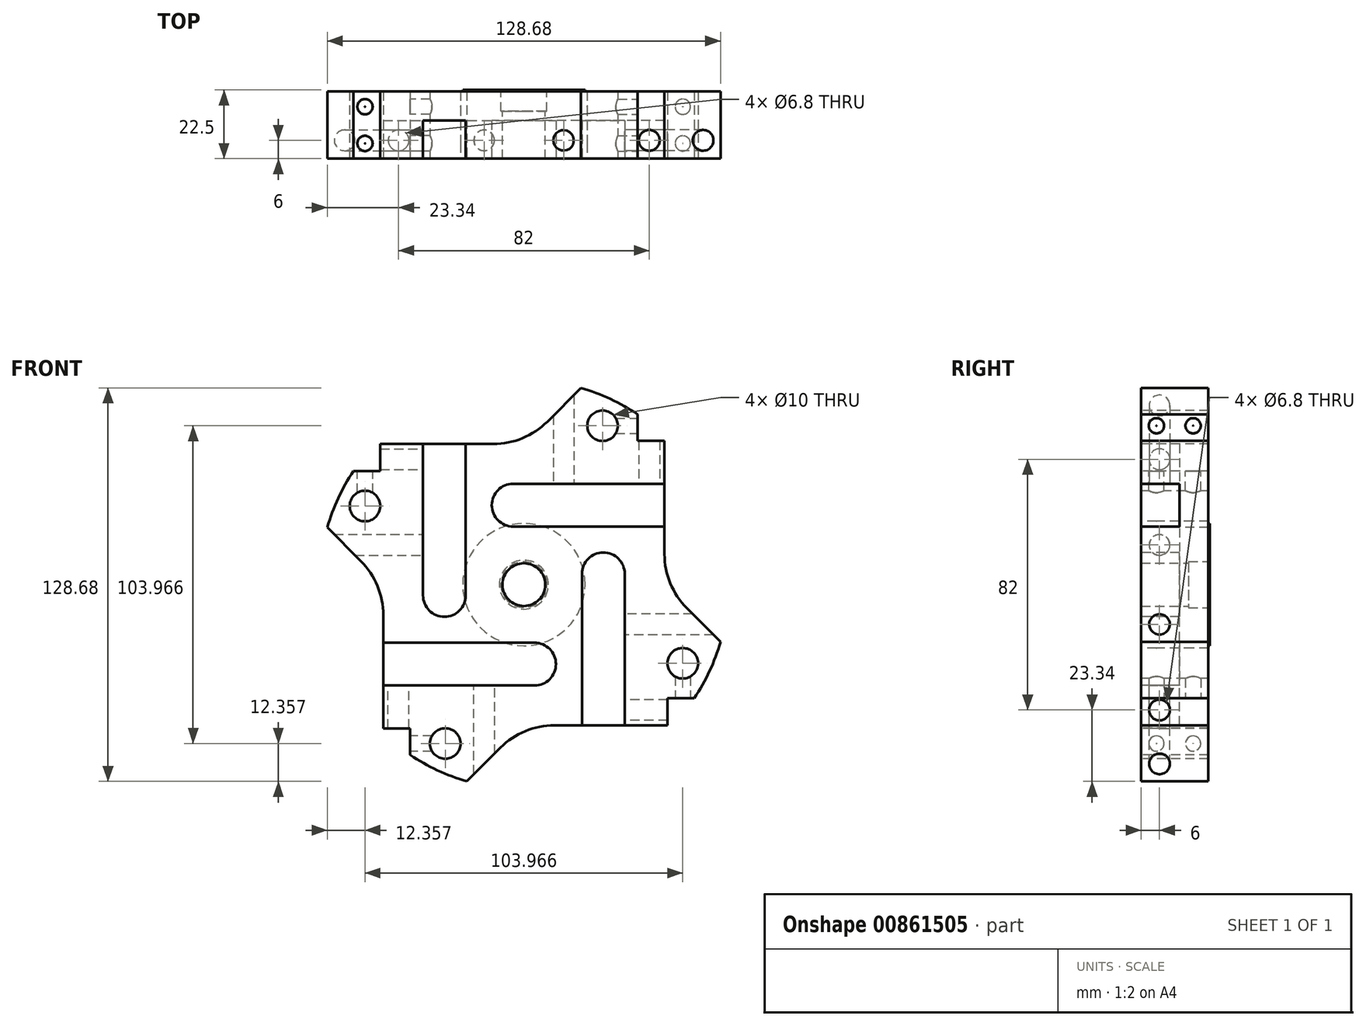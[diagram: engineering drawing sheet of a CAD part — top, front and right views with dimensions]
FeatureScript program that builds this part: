
annotation { "Feature Type Name" : "Feature", "Feature Type Description" : "" }
export const myFeature = defineFeature(function(context is Context, id is Id, definition is map)
    precondition{}
    {
        {
            var Q0;
            Q0=qCreatedBy(makeId("Front.planeOp"),FACE);
            var sketch = newSketch(context, id + "F0", { "sketchPlane" : qUnion([Q0])});
            skLineSegment(sketch, "E0", {"start": v(-46, -10) * mm, "end": v(-46, -47) * mm});
            skLineSegment(sketch, "E1", {"start": v(-37.2, -47) * mm, "end": v(-37.2, -55.72) * mm});
            skLineSegment(sketch, "E2", {"start": v(-46, -47) * mm, "end": v(-37.2, -47) * mm});
            skArc(sketch, "E3.trimOffspring", {"start": v(-46, -10) * mm, "mid": v(-47.9, -0.43) * mm, "end": v(-53.32, 7.68) * mm});
            skLineSegment(sketch, "E4", {"start": v(-53.32, 7.68) * mm, "end": v(-64.34, 18.7) * mm});
            skArc(sketch, "E5", {"start": v(-37.2, -55.72) * mm, "mid": v(-28.28, -60.74) * mm, "end": v(-18.7, -64.34) * mm});
            skLineSegment(sketch, "E6", {"start": v(-71, -10) * mm, "end": v(-46, -10) * mm, "construction": true});
            skLineSegment(sketch, "E7", {"start": v(-71, -10) * mm, "end": v(-53.32, 7.68) * mm, "construction": true});
            skLineSegment(sketch, "E8.1.0", {"start": v(-7.68, -53.32) * mm, "end": v(-18.7, -64.34) * mm});
            skArc(sketch, "E8.1.1", {"start": v(10, -46) * mm, "mid": v(0.43, -47.9) * mm, "end": v(-7.68, -53.32) * mm});
            skLineSegment(sketch, "E8.1.2", {"start": v(10, -46) * mm, "end": v(47, -46) * mm});
            skLineSegment(sketch, "E8.1.3", {"start": v(47, -46) * mm, "end": v(47, -37.2) * mm});
            skLineSegment(sketch, "E8.1.4", {"start": v(47, -37.2) * mm, "end": v(55.72, -37.2) * mm});
            skLineSegment(sketch, "E8.2.0", {"start": v(53.32, -7.68) * mm, "end": v(64.34, -18.7) * mm});
            skArc(sketch, "E8.2.1", {"start": v(46, 10) * mm, "mid": v(47.9, 0.43) * mm, "end": v(53.32, -7.68) * mm});
            skLineSegment(sketch, "E8.2.2", {"start": v(46, 10) * mm, "end": v(46, 47) * mm});
            skLineSegment(sketch, "E8.2.3", {"start": v(46, 47) * mm, "end": v(37.2, 47) * mm});
            skLineSegment(sketch, "E8.2.4", {"start": v(37.2, 47) * mm, "end": v(37.2, 55.72) * mm});
            skLineSegment(sketch, "E8.3.0", {"start": v(7.68, 53.32) * mm, "end": v(18.7, 64.34) * mm});
            skArc(sketch, "E8.3.1", {"start": v(-10, 46) * mm, "mid": v(-0.43, 47.9) * mm, "end": v(7.68, 53.32) * mm});
            skLineSegment(sketch, "E8.3.2", {"start": v(-10, 46) * mm, "end": v(-47, 46) * mm});
            skLineSegment(sketch, "E8.3.3", {"start": v(-47, 46) * mm, "end": v(-47, 37.2) * mm});
            skLineSegment(sketch, "E8.3.4", {"start": v(-47, 37.2) * mm, "end": v(-55.72, 37.2) * mm});
            skArc(sketch, "E9.trimOffspring", {"start": v(-55.72, 37.2) * mm, "mid": v(-60.74, 28.28) * mm, "end": v(-64.34, 18.7) * mm});
            skArc(sketch, "E10.trimOffspring", {"start": v(37.2, 55.72) * mm, "mid": v(28.28, 60.74) * mm, "end": v(18.7, 64.34) * mm});
            skArc(sketch, "E11.trimOffspring", {"start": v(55.72, -37.2) * mm, "mid": v(60.74, -28.28) * mm, "end": v(64.34, -18.7) * mm});
            skLineSegment(sketch, "E12", {"start": v(0, 0) * mm, "end": v(-51.98, 25.73) * mm});
            skCircle(sketch, "E13", {"center": v(-51.98, 25.73) * mm, "radius": 5 * mm});
            skCircle(sketch, "E14.1.0", {"center": v(-25.73, -51.98) * mm, "radius": 5 * mm});
            skCircle(sketch, "E14.2.0", {"center": v(51.98, -25.73) * mm, "radius": 5 * mm});
            skCircle(sketch, "E14.3.0", {"center": v(25.73, 51.98) * mm, "radius": 5 * mm});
            skSolve(sketch);
        }
        {
            var Q0;
            Q0 = qSketchRegion(id + "F0", true);
            extrude(context, id + "F1", {"entities" : qUnion([Q0]), "oppositeDirection" : true, "depth" : 22 * mm, "offsetDistance" : 25 * mm});
        }
        {
            var Q0;
            Q0=makeQuery(id+"F1.opExtrude","CAP_FACE",FACE,{"disambiguationData":[OSD([sQuery(id+"F0.wireOp",EDGE,"E0"),sQuery(id+"F0.wireOp",EDGE,"E1"),sQuery(id+"F0.wireOp",EDGE,"E2"),sQuery(id+"F0.wireOp",EDGE,"E3.trimOffspring"),sQuery(id+"F0.wireOp",EDGE,"E4"),sQuery(id+"F0.wireOp",EDGE,"E5"),sQuery(id+"F0.wireOp",EDGE,"E8.1.0"),sQuery(id+"F0.wireOp",EDGE,"E8.1.1"),sQuery(id+"F0.wireOp",EDGE,"E8.1.2"),sQuery(id+"F0.wireOp",EDGE,"E8.1.3"),sQuery(id+"F0.wireOp",EDGE,"E8.1.4"),sQuery(id+"F0.wireOp",EDGE,"E8.2.0"),sQuery(id+"F0.wireOp",EDGE,"E8.2.1"),sQuery(id+"F0.wireOp",EDGE,"E8.2.2"),sQuery(id+"F0.wireOp",EDGE,"E8.2.3"),sQuery(id+"F0.wireOp",EDGE,"E8.2.4"),sQuery(id+"F0.wireOp",EDGE,"E8.3.0"),sQuery(id+"F0.wireOp",EDGE,"E8.3.1"),sQuery(id+"F0.wireOp",EDGE,"E8.3.2"),sQuery(id+"F0.wireOp",EDGE,"E8.3.3"),sQuery(id+"F0.wireOp",EDGE,"E8.3.4"),sQuery(id+"F0.wireOp",EDGE,"E9.trimOffspring"),sQuery(id+"F0.wireOp",EDGE,"E10.trimOffspring"),sQuery(id+"F0.wireOp",EDGE,"E11.trimOffspring"),sQuery(id+"F0.wireOp",EDGE,"E13"),sQuery(id+"F0.wireOp",EDGE,"E14.1.0"),sQuery(id+"F0.wireOp",EDGE,"E14.2.0"),sQuery(id+"F0.wireOp",EDGE,"E14.3.0")])],"isStart":false});
            var sketch = newSketch(context, id + "F2", { "sketchPlane" : qUnion([Q0])});
            skCircle(sketch, "E15", {"center": v(0, 0) * mm, "radius": 20 * mm});
            skSolve(sketch);
        }
        {
            var Q0;
            Q0 = qSketchRegion(id + "F2", true);
            extrude(context, id + "F3", {"entities" : qUnion([Q0]), "operationType" : NewBodyOperationType.ADD, "depth" : .5 * mm, "offsetDistance" : 25 * mm});
        }
        {
            var Q0;
            Q0=makeQuery(id+"F1.opExtrude","SWEPT_FACE",FACE,{"disambiguationData":[OSD([sQuery(id+"F0.wireOp",EDGE,"E8.2.4")])]});
            var sketch = newSketch(context, id + "F4", { "sketchPlane" : qUnion([Q0])});
            skPoint(sketch, "E16", {"position": v(5, 51.98) * mm});
            skPoint(sketch, "E17", {"position": v(17, 51.98) * mm});
            skSolve(sketch);
        }
        {
            var Q0;
            Q0=sQuery(id+"F4.wireOp",VERTEX,"E16");
            var Q1;
            Q1=sQuery(id+"F4.wireOp",VERTEX,"E17");
            var Q2;
            Q2=makeQuery(id+"F1.opExtrude","SWEPT_BODY",BODY,{"disambiguationData":[OSD([sQuery(id+"F0.wireOp",EDGE,"E0"),sQuery(id+"F0.wireOp",EDGE,"E1"),sQuery(id+"F0.wireOp",EDGE,"E2"),sQuery(id+"F0.wireOp",EDGE,"E3.trimOffspring"),sQuery(id+"F0.wireOp",EDGE,"E4"),sQuery(id+"F0.wireOp",EDGE,"E5"),sQuery(id+"F0.wireOp",EDGE,"E8.1.0"),sQuery(id+"F0.wireOp",EDGE,"E8.1.1"),sQuery(id+"F0.wireOp",EDGE,"E8.1.2"),sQuery(id+"F0.wireOp",EDGE,"E8.1.3"),sQuery(id+"F0.wireOp",EDGE,"E8.1.4"),sQuery(id+"F0.wireOp",EDGE,"E8.2.0"),sQuery(id+"F0.wireOp",EDGE,"E8.2.1"),sQuery(id+"F0.wireOp",EDGE,"E8.2.2"),sQuery(id+"F0.wireOp",EDGE,"E8.2.3"),sQuery(id+"F0.wireOp",EDGE,"E8.2.4"),sQuery(id+"F0.wireOp",EDGE,"E8.3.0"),sQuery(id+"F0.wireOp",EDGE,"E8.3.1"),sQuery(id+"F0.wireOp",EDGE,"E8.3.2"),sQuery(id+"F0.wireOp",EDGE,"E8.3.3"),sQuery(id+"F0.wireOp",EDGE,"E8.3.4"),sQuery(id+"F0.wireOp",EDGE,"E9.trimOffspring"),sQuery(id+"F0.wireOp",EDGE,"E10.trimOffspring"),sQuery(id+"F0.wireOp",EDGE,"E11.trimOffspring"),sQuery(id+"F0.wireOp",EDGE,"E13"),sQuery(id+"F0.wireOp",EDGE,"E14.1.0"),sQuery(id+"F0.wireOp",EDGE,"E14.2.0"),sQuery(id+"F0.wireOp",EDGE,"E14.3.0")])]});
            hole(context, id + "F5", {"style" : HoleStyle.SIMPLE, "endStyle" : HoleEndStyle.BLIND, "standardTappedOrClearance" : lookupTablePath({ "standard" : "ISO", "engagement" : "75%", "pitch" : "1 mm", "size" : "M6", "type" : "Tapped" }), "standardBlindInLast" : lookupTablePath({ "standard" : "ISO", "engagement" : "75%", "pitch" : "1 mm", "size" : "M6", "type" : "Tapped" }), "holeDiameter" : 5 * mm, "majorDiameter" : 6 * mm, "showTappedDepth" : true, "holeDepth" : 15 * mm, "isTappedThrough" : true, "tappedDepth" : 12 * mm, "tapClearance" : 3, "startFromSketch" : true, "locations" : qUnion([Q0, Q1]), "scope" : qUnion([Q2])});
        }
        {
            var Q0;
            Q0=makeQuery(id+"F1.opExtrude","SWEPT_FACE",FACE,{"disambiguationData":[OSD([sQuery(id+"F0.wireOp",EDGE,"E8.3.4")])]});
            var sketch = newSketch(context, id + "F6", { "sketchPlane" : qUnion([Q0])});
            skPoint(sketch, "E18", {"position": v(-51.98, 5) * mm});
            skPoint(sketch, "E19", {"position": v(-51.98, 17) * mm});
            skSolve(sketch);
        }
        {
            var Q0;
            Q0=sQuery(id+"F6.wireOp",VERTEX,"E19");
            var Q1;
            Q1=sQuery(id+"F6.wireOp",VERTEX,"E18");
            var Q2;
            Q2=makeQuery(id+"F1.opExtrude","SWEPT_BODY",BODY,{"disambiguationData":[OSD([sQuery(id+"F0.wireOp",EDGE,"E0"),sQuery(id+"F0.wireOp",EDGE,"E1"),sQuery(id+"F0.wireOp",EDGE,"E2"),sQuery(id+"F0.wireOp",EDGE,"E3.trimOffspring"),sQuery(id+"F0.wireOp",EDGE,"E4"),sQuery(id+"F0.wireOp",EDGE,"E5"),sQuery(id+"F0.wireOp",EDGE,"E8.1.0"),sQuery(id+"F0.wireOp",EDGE,"E8.1.1"),sQuery(id+"F0.wireOp",EDGE,"E8.1.2"),sQuery(id+"F0.wireOp",EDGE,"E8.1.3"),sQuery(id+"F0.wireOp",EDGE,"E8.1.4"),sQuery(id+"F0.wireOp",EDGE,"E8.2.0"),sQuery(id+"F0.wireOp",EDGE,"E8.2.1"),sQuery(id+"F0.wireOp",EDGE,"E8.2.2"),sQuery(id+"F0.wireOp",EDGE,"E8.2.3"),sQuery(id+"F0.wireOp",EDGE,"E8.2.4"),sQuery(id+"F0.wireOp",EDGE,"E8.3.0"),sQuery(id+"F0.wireOp",EDGE,"E8.3.1"),sQuery(id+"F0.wireOp",EDGE,"E8.3.2"),sQuery(id+"F0.wireOp",EDGE,"E8.3.3"),sQuery(id+"F0.wireOp",EDGE,"E8.3.4"),sQuery(id+"F0.wireOp",EDGE,"E9.trimOffspring"),sQuery(id+"F0.wireOp",EDGE,"E10.trimOffspring"),sQuery(id+"F0.wireOp",EDGE,"E11.trimOffspring"),sQuery(id+"F0.wireOp",EDGE,"E13"),sQuery(id+"F0.wireOp",EDGE,"E14.1.0"),sQuery(id+"F0.wireOp",EDGE,"E14.2.0"),sQuery(id+"F0.wireOp",EDGE,"E14.3.0")])]});
            hole(context, id + "F7", {"style" : HoleStyle.SIMPLE, "endStyle" : HoleEndStyle.BLIND, "standardTappedOrClearance" : lookupTablePath({ "standard" : "ISO", "engagement" : "75%", "pitch" : "1 mm", "size" : "M6", "type" : "Tapped" }), "standardBlindInLast" : lookupTablePath({ "standard" : "ISO", "engagement" : "75%", "pitch" : "1 mm", "size" : "M6", "type" : "Tapped" }), "holeDiameter" : 5 * mm, "majorDiameter" : 6 * mm, "showTappedDepth" : true, "holeDepth" : 15 * mm, "isTappedThrough" : true, "tappedDepth" : 12 * mm, "tapClearance" : 3, "startFromSketch" : true, "locations" : qUnion([Q0, Q1]), "scope" : qUnion([Q2])});
        }
        {
            var Q0;
            Q0=makeQuery(id+"F1.opExtrude","SWEPT_FACE",FACE,{"disambiguationData":[OSD([sQuery(id+"F0.wireOp",EDGE,"E1")])]});
            var sketch = newSketch(context, id + "F8", { "sketchPlane" : qUnion([Q0])});
            skPoint(sketch, "E20", {"position": v(-5, -51.98) * mm});
            skPoint(sketch, "E21", {"position": v(-17, -51.98) * mm});
            skSolve(sketch);
        }
        {
            var Q0;
            Q0=sQuery(id+"F8.wireOp",VERTEX,"E20");
            var Q1;
            Q1=sQuery(id+"F8.wireOp",VERTEX,"E21");
            var Q2;
            Q2=makeQuery(id+"F1.opExtrude","SWEPT_BODY",BODY,{"disambiguationData":[OSD([sQuery(id+"F0.wireOp",EDGE,"E0"),sQuery(id+"F0.wireOp",EDGE,"E1"),sQuery(id+"F0.wireOp",EDGE,"E2"),sQuery(id+"F0.wireOp",EDGE,"E3.trimOffspring"),sQuery(id+"F0.wireOp",EDGE,"E4"),sQuery(id+"F0.wireOp",EDGE,"E5"),sQuery(id+"F0.wireOp",EDGE,"E8.1.0"),sQuery(id+"F0.wireOp",EDGE,"E8.1.1"),sQuery(id+"F0.wireOp",EDGE,"E8.1.2"),sQuery(id+"F0.wireOp",EDGE,"E8.1.3"),sQuery(id+"F0.wireOp",EDGE,"E8.1.4"),sQuery(id+"F0.wireOp",EDGE,"E8.2.0"),sQuery(id+"F0.wireOp",EDGE,"E8.2.1"),sQuery(id+"F0.wireOp",EDGE,"E8.2.2"),sQuery(id+"F0.wireOp",EDGE,"E8.2.3"),sQuery(id+"F0.wireOp",EDGE,"E8.2.4"),sQuery(id+"F0.wireOp",EDGE,"E8.3.0"),sQuery(id+"F0.wireOp",EDGE,"E8.3.1"),sQuery(id+"F0.wireOp",EDGE,"E8.3.2"),sQuery(id+"F0.wireOp",EDGE,"E8.3.3"),sQuery(id+"F0.wireOp",EDGE,"E8.3.4"),sQuery(id+"F0.wireOp",EDGE,"E9.trimOffspring"),sQuery(id+"F0.wireOp",EDGE,"E10.trimOffspring"),sQuery(id+"F0.wireOp",EDGE,"E11.trimOffspring"),sQuery(id+"F0.wireOp",EDGE,"E13"),sQuery(id+"F0.wireOp",EDGE,"E14.1.0"),sQuery(id+"F0.wireOp",EDGE,"E14.2.0"),sQuery(id+"F0.wireOp",EDGE,"E14.3.0")])]});
            hole(context, id + "F9", {"style" : HoleStyle.SIMPLE, "endStyle" : HoleEndStyle.BLIND, "standardTappedOrClearance" : lookupTablePath({ "standard" : "ISO", "engagement" : "75%", "pitch" : "1 mm", "size" : "M6", "type" : "Tapped" }), "standardBlindInLast" : lookupTablePath({ "standard" : "ISO", "engagement" : "75%", "pitch" : "1 mm", "size" : "M6", "type" : "Tapped" }), "holeDiameter" : 5 * mm, "majorDiameter" : 6 * mm, "showTappedDepth" : true, "holeDepth" : 15 * mm, "isTappedThrough" : true, "tappedDepth" : 12 * mm, "tapClearance" : 3, "startFromSketch" : true, "locations" : qUnion([Q0, Q1]), "scope" : qUnion([Q2])});
        }
        {
            var Q0;
            Q0=makeQuery(id+"F1.opExtrude","SWEPT_FACE",FACE,{"disambiguationData":[OSD([sQuery(id+"F0.wireOp",EDGE,"E8.1.4")])]});
            var sketch = newSketch(context, id + "F10", { "sketchPlane" : qUnion([Q0])});
            skPoint(sketch, "E22", {"position": v(51.98, -5) * mm});
            skPoint(sketch, "E23", {"position": v(51.98, -17) * mm});
            skSolve(sketch);
        }
        {
            var Q0;
            Q0=sQuery(id+"F10.wireOp",VERTEX,"E22");
            var Q1;
            Q1=sQuery(id+"F10.wireOp",VERTEX,"E23");
            var Q2;
            Q2=makeQuery(id+"F1.opExtrude","SWEPT_BODY",BODY,{"disambiguationData":[OSD([sQuery(id+"F0.wireOp",EDGE,"E0"),sQuery(id+"F0.wireOp",EDGE,"E1"),sQuery(id+"F0.wireOp",EDGE,"E2"),sQuery(id+"F0.wireOp",EDGE,"E3.trimOffspring"),sQuery(id+"F0.wireOp",EDGE,"E4"),sQuery(id+"F0.wireOp",EDGE,"E5"),sQuery(id+"F0.wireOp",EDGE,"E8.1.0"),sQuery(id+"F0.wireOp",EDGE,"E8.1.1"),sQuery(id+"F0.wireOp",EDGE,"E8.1.2"),sQuery(id+"F0.wireOp",EDGE,"E8.1.3"),sQuery(id+"F0.wireOp",EDGE,"E8.1.4"),sQuery(id+"F0.wireOp",EDGE,"E8.2.0"),sQuery(id+"F0.wireOp",EDGE,"E8.2.1"),sQuery(id+"F0.wireOp",EDGE,"E8.2.2"),sQuery(id+"F0.wireOp",EDGE,"E8.2.3"),sQuery(id+"F0.wireOp",EDGE,"E8.2.4"),sQuery(id+"F0.wireOp",EDGE,"E8.3.0"),sQuery(id+"F0.wireOp",EDGE,"E8.3.1"),sQuery(id+"F0.wireOp",EDGE,"E8.3.2"),sQuery(id+"F0.wireOp",EDGE,"E8.3.3"),sQuery(id+"F0.wireOp",EDGE,"E8.3.4"),sQuery(id+"F0.wireOp",EDGE,"E9.trimOffspring"),sQuery(id+"F0.wireOp",EDGE,"E10.trimOffspring"),sQuery(id+"F0.wireOp",EDGE,"E11.trimOffspring"),sQuery(id+"F0.wireOp",EDGE,"E13"),sQuery(id+"F0.wireOp",EDGE,"E14.1.0"),sQuery(id+"F0.wireOp",EDGE,"E14.2.0"),sQuery(id+"F0.wireOp",EDGE,"E14.3.0")])]});
            hole(context, id + "F11", {"style" : HoleStyle.SIMPLE, "endStyle" : HoleEndStyle.BLIND, "standardTappedOrClearance" : lookupTablePath({ "standard" : "ISO", "engagement" : "75%", "pitch" : "1 mm", "size" : "M6", "type" : "Tapped" }), "standardBlindInLast" : lookupTablePath({ "standard" : "ISO", "engagement" : "75%", "pitch" : "1 mm", "size" : "M6", "type" : "Tapped" }), "holeDiameter" : 5 * mm, "majorDiameter" : 6 * mm, "showTappedDepth" : true, "holeDepth" : 15 * mm, "isTappedThrough" : true, "tappedDepth" : 12 * mm, "tapClearance" : 3, "startFromSketch" : true, "locations" : qUnion([Q0, Q1]), "scope" : qUnion([Q2])});
        }
        {
            var Q0;
            Q0=makeQuery(id+"F1.opExtrude","CAP_FACE",FACE,{"disambiguationData":[OSD([sQuery(id+"F0.wireOp",EDGE,"E0"),sQuery(id+"F0.wireOp",EDGE,"E1"),sQuery(id+"F0.wireOp",EDGE,"E2"),sQuery(id+"F0.wireOp",EDGE,"E3.trimOffspring"),sQuery(id+"F0.wireOp",EDGE,"E4"),sQuery(id+"F0.wireOp",EDGE,"E5"),sQuery(id+"F0.wireOp",EDGE,"E8.1.0"),sQuery(id+"F0.wireOp",EDGE,"E8.1.1"),sQuery(id+"F0.wireOp",EDGE,"E8.1.2"),sQuery(id+"F0.wireOp",EDGE,"E8.1.3"),sQuery(id+"F0.wireOp",EDGE,"E8.1.4"),sQuery(id+"F0.wireOp",EDGE,"E8.2.0"),sQuery(id+"F0.wireOp",EDGE,"E8.2.1"),sQuery(id+"F0.wireOp",EDGE,"E8.2.2"),sQuery(id+"F0.wireOp",EDGE,"E8.2.3"),sQuery(id+"F0.wireOp",EDGE,"E8.2.4"),sQuery(id+"F0.wireOp",EDGE,"E8.3.0"),sQuery(id+"F0.wireOp",EDGE,"E8.3.1"),sQuery(id+"F0.wireOp",EDGE,"E8.3.2"),sQuery(id+"F0.wireOp",EDGE,"E8.3.3"),sQuery(id+"F0.wireOp",EDGE,"E8.3.4"),sQuery(id+"F0.wireOp",EDGE,"E9.trimOffspring"),sQuery(id+"F0.wireOp",EDGE,"E10.trimOffspring"),sQuery(id+"F0.wireOp",EDGE,"E11.trimOffspring"),sQuery(id+"F0.wireOp",EDGE,"E13"),sQuery(id+"F0.wireOp",EDGE,"E14.1.0"),sQuery(id+"F0.wireOp",EDGE,"E14.2.0"),sQuery(id+"F0.wireOp",EDGE,"E14.3.0")])],"isStart":true});
            var sketch = newSketch(context, id + "F12", { "sketchPlane" : qUnion([Q0])});
            skLineSegment(sketch, "E24", {"start": v(19, -46) * mm, "end": v(19, 3.5) * mm});
            skLineSegment(sketch, "E25", {"start": v(26, 10.5) * mm, "end": v(26, 10.5) * mm});
            skLineSegment(sketch, "E26", {"start": v(33, 3.5) * mm, "end": v(33, -46) * mm});
            skLineSegment(sketch, "E27", {"start": v(33, -46) * mm, "end": v(19, -46) * mm});
            skPoint(sketch, "E28.visualSharp", {"position": v(19, 10.5) * mm});
            skArc(sketch, "E28.filletArc", {"start": v(26, 10.5) * mm, "mid": v(21.05, 8.45) * mm, "end": v(19, 3.5) * mm});
            skPoint(sketch, "E29.visualSharp", {"position": v(33, 10.5) * mm});
            skArc(sketch, "E29.filletArc", {"start": v(33, 3.5) * mm, "mid": v(30.95, 8.45) * mm, "end": v(26, 10.5) * mm});
            skLineSegment(sketch, "E30.1.0", {"start": v(46, 19) * mm, "end": v(-3.5, 19) * mm});
            skLineSegment(sketch, "E30.1.1", {"start": v(46, 33) * mm, "end": v(46, 19) * mm});
            skLineSegment(sketch, "E30.1.2", {"start": v(-3.5, 33) * mm, "end": v(46, 33) * mm});
            skArc(sketch, "E30.1.3", {"start": v(-3.5, 33) * mm, "mid": v(-8.45, 30.95) * mm, "end": v(-10.5, 26) * mm});
            skArc(sketch, "E30.1.4", {"start": v(-10.5, 26) * mm, "mid": v(-8.45, 21.05) * mm, "end": v(-3.5, 19) * mm});
            skLineSegment(sketch, "E30.2.0", {"start": v(-19, 46) * mm, "end": v(-19, -3.5) * mm});
            skLineSegment(sketch, "E30.2.1", {"start": v(-33, 46) * mm, "end": v(-19, 46) * mm});
            skLineSegment(sketch, "E30.2.2", {"start": v(-33, -3.5) * mm, "end": v(-33, 46) * mm});
            skArc(sketch, "E30.2.3", {"start": v(-33, -3.5) * mm, "mid": v(-30.95, -8.45) * mm, "end": v(-26, -10.5) * mm});
            skArc(sketch, "E30.2.4", {"start": v(-26, -10.5) * mm, "mid": v(-21.05, -8.45) * mm, "end": v(-19, -3.5) * mm});
            skLineSegment(sketch, "E30.3.0", {"start": v(-46, -19) * mm, "end": v(3.5, -19) * mm});
            skLineSegment(sketch, "E30.3.1", {"start": v(-46, -33) * mm, "end": v(-46, -19) * mm});
            skLineSegment(sketch, "E30.3.2", {"start": v(3.5, -33) * mm, "end": v(-46, -33) * mm});
            skArc(sketch, "E30.3.3", {"start": v(3.5, -33) * mm, "mid": v(8.45, -30.95) * mm, "end": v(10.5, -26) * mm});
            skArc(sketch, "E30.3.4", {"start": v(10.5, -26) * mm, "mid": v(8.45, -21.05) * mm, "end": v(3.5, -19) * mm});
            skPoint(sketch, "E30.center", {"position": v(0, 0) * mm});
            skSolve(sketch);
        }
        {
            var Q0;
            Q0 = qSketchRegion(id + "F12", true);
            extrude(context, id + "F13", {"entities" : qUnion([Q0]), "operationType" : NewBodyOperationType.REMOVE, "oppositeDirection" : true, "depth" : 12.5 * mm, "offsetDistance" : 25 * mm});
        }
        {
            var Q0;
            Q0=makeQuery(id+"F13.boolean.opBoolean","COPY",FACE,{"derivedFrom":makeQuery(id+"F13.opExtrude","SWEPT_FACE",FACE,{"disambiguationData":[OSD([sQuery(id+"F12.wireOp",EDGE,"E30.2.2")])]})});
            var sketch = newSketch(context, id + "F14", { "sketchPlane" : qUnion([Q0])});
            skPoint(sketch, "E31", {"position": v(6, 13) * mm});
            skPoint(sketch, "E32", {"position": v(6, 41) * mm});
            skSolve(sketch);
        }
        {
            var Q0;
            Q0=makeQuery(id+"F13.boolean.opBoolean","COPY",FACE,{"derivedFrom":makeQuery(id+"F13.opExtrude","SWEPT_FACE",FACE,{"disambiguationData":[OSD([sQuery(id+"F12.wireOp",EDGE,"E30.3.2")])]})});
            var sketch = newSketch(context, id + "F15", { "sketchPlane" : qUnion([Q0])});
            skPoint(sketch, "E33", {"position": v(-13, 6) * mm});
            skPoint(sketch, "E34", {"position": v(-41, 6) * mm});
            skSolve(sketch);
        }
        {
            var Q0;
            Q0=makeQuery(id+"F13.boolean.opBoolean","COPY",FACE,{"derivedFrom":makeQuery(id+"F13.opExtrude","SWEPT_FACE",FACE,{"disambiguationData":[OSD([sQuery(id+"F12.wireOp",EDGE,"E26")])]})});
            var sketch = newSketch(context, id + "F16", { "sketchPlane" : qUnion([Q0])});
            skPoint(sketch, "E35", {"position": v(-6, -13) * mm});
            skPoint(sketch, "E36", {"position": v(-6, -41) * mm});
            skSolve(sketch);
        }
        {
            var Q0;
            Q0=makeQuery(id+"F13.boolean.opBoolean","COPY",FACE,{"derivedFrom":makeQuery(id+"F13.opExtrude","SWEPT_FACE",FACE,{"disambiguationData":[OSD([sQuery(id+"F12.wireOp",EDGE,"E30.1.2")])]})});
            var sketch = newSketch(context, id + "F17", { "sketchPlane" : qUnion([Q0])});
            skPoint(sketch, "E37", {"position": v(13, -6) * mm});
            skPoint(sketch, "E38", {"position": v(41, -6) * mm});
            skSolve(sketch);
        }
        {
            var Q0;
            Q0=sQuery(id+"F14.wireOp",VERTEX,"E32");
            var Q1;
            Q1=sQuery(id+"F14.wireOp",VERTEX,"E31");
            var Q2;
            Q2=sQuery(id+"F15.wireOp",VERTEX,"E34");
            var Q3;
            Q3=sQuery(id+"F15.wireOp",VERTEX,"E33");
            var Q4;
            Q4=sQuery(id+"F16.wireOp",VERTEX,"E36");
            var Q5;
            Q5=sQuery(id+"F16.wireOp",VERTEX,"E35");
            var Q6;
            Q6=sQuery(id+"F17.wireOp",VERTEX,"E38");
            var Q7;
            Q7=sQuery(id+"F17.wireOp",VERTEX,"E37");
            var Q8;
            Q8=makeQuery(id+"F1.opExtrude","SWEPT_BODY",BODY,{"disambiguationData":[OSD([sQuery(id+"F0.wireOp",EDGE,"E0"),sQuery(id+"F0.wireOp",EDGE,"E1"),sQuery(id+"F0.wireOp",EDGE,"E2"),sQuery(id+"F0.wireOp",EDGE,"E3.trimOffspring"),sQuery(id+"F0.wireOp",EDGE,"E4"),sQuery(id+"F0.wireOp",EDGE,"E5"),sQuery(id+"F0.wireOp",EDGE,"E8.1.0"),sQuery(id+"F0.wireOp",EDGE,"E8.1.1"),sQuery(id+"F0.wireOp",EDGE,"E8.1.2"),sQuery(id+"F0.wireOp",EDGE,"E8.1.3"),sQuery(id+"F0.wireOp",EDGE,"E8.1.4"),sQuery(id+"F0.wireOp",EDGE,"E8.2.0"),sQuery(id+"F0.wireOp",EDGE,"E8.2.1"),sQuery(id+"F0.wireOp",EDGE,"E8.2.2"),sQuery(id+"F0.wireOp",EDGE,"E8.2.3"),sQuery(id+"F0.wireOp",EDGE,"E8.2.4"),sQuery(id+"F0.wireOp",EDGE,"E8.3.0"),sQuery(id+"F0.wireOp",EDGE,"E8.3.1"),sQuery(id+"F0.wireOp",EDGE,"E8.3.2"),sQuery(id+"F0.wireOp",EDGE,"E8.3.3"),sQuery(id+"F0.wireOp",EDGE,"E8.3.4"),sQuery(id+"F0.wireOp",EDGE,"E9.trimOffspring"),sQuery(id+"F0.wireOp",EDGE,"E10.trimOffspring"),sQuery(id+"F0.wireOp",EDGE,"E11.trimOffspring"),sQuery(id+"F0.wireOp",EDGE,"E13"),sQuery(id+"F0.wireOp",EDGE,"E14.1.0"),sQuery(id+"F0.wireOp",EDGE,"E14.2.0"),sQuery(id+"F0.wireOp",EDGE,"E14.3.0")])]});
            hole(context, id + "F18", {"style" : HoleStyle.SIMPLE, "endStyle" : HoleEndStyle.BLIND, "standardTappedOrClearance" : lookupTablePath({ "standard" : "ISO", "engagement" : "75%", "pitch" : "1.25 mm", "size" : "M8", "type" : "Tapped" }), "standardBlindInLast" : lookupTablePath({ "standard" : "ISO", "engagement" : "75%", "pitch" : "1.25 mm", "size" : "M8", "type" : "Tapped" }), "holeDiameter" : 6.8 * mm, "majorDiameter" : 8 * mm, "showTappedDepth" : true, "holeDepth" : 35 * mm, "isTappedThrough" : true, "tappedDepth" : 31.25 * mm, "tapClearance" : 3, "startFromSketch" : true, "locations" : qUnion([Q0, Q1, Q2, Q3, Q4, Q5, Q6, Q7]), "scope" : qUnion([Q8])});
        }
        {
            var Q0;
            Q0=makeQuery(id+"F3.opExtrude","CAP_FACE",FACE,{"disambiguationData":[OSD([sQuery(id+"F2.wireOp",EDGE,"E15")])],"isStart":false});
            var sketch = newSketch(context, id + "F19", { "sketchPlane" : qUnion([Q0])});
            skPoint(sketch, "E39", {"position": v(0, 0) * mm});
            skSolve(sketch);
        }
        {
            var Q0;
            Q0=sQuery(id+"F19.wireOp",VERTEX,"E39");
            var Q1;
            Q1=makeQuery(id+"F1.opExtrude","SWEPT_BODY",BODY,{"disambiguationData":[OSD([sQuery(id+"F0.wireOp",EDGE,"E0"),sQuery(id+"F0.wireOp",EDGE,"E1"),sQuery(id+"F0.wireOp",EDGE,"E2"),sQuery(id+"F0.wireOp",EDGE,"E3.trimOffspring"),sQuery(id+"F0.wireOp",EDGE,"E4"),sQuery(id+"F0.wireOp",EDGE,"E5"),sQuery(id+"F0.wireOp",EDGE,"E8.1.0"),sQuery(id+"F0.wireOp",EDGE,"E8.1.1"),sQuery(id+"F0.wireOp",EDGE,"E8.1.2"),sQuery(id+"F0.wireOp",EDGE,"E8.1.3"),sQuery(id+"F0.wireOp",EDGE,"E8.1.4"),sQuery(id+"F0.wireOp",EDGE,"E8.2.0"),sQuery(id+"F0.wireOp",EDGE,"E8.2.1"),sQuery(id+"F0.wireOp",EDGE,"E8.2.2"),sQuery(id+"F0.wireOp",EDGE,"E8.2.3"),sQuery(id+"F0.wireOp",EDGE,"E8.2.4"),sQuery(id+"F0.wireOp",EDGE,"E8.3.0"),sQuery(id+"F0.wireOp",EDGE,"E8.3.1"),sQuery(id+"F0.wireOp",EDGE,"E8.3.2"),sQuery(id+"F0.wireOp",EDGE,"E8.3.3"),sQuery(id+"F0.wireOp",EDGE,"E8.3.4"),sQuery(id+"F0.wireOp",EDGE,"E9.trimOffspring"),sQuery(id+"F0.wireOp",EDGE,"E10.trimOffspring"),sQuery(id+"F0.wireOp",EDGE,"E11.trimOffspring"),sQuery(id+"F0.wireOp",EDGE,"E13"),sQuery(id+"F0.wireOp",EDGE,"E14.1.0"),sQuery(id+"F0.wireOp",EDGE,"E14.2.0"),sQuery(id+"F0.wireOp",EDGE,"E14.3.0")])]});
            hole(context, id + "F20", {"style" : HoleStyle.C_SINK, "endStyle" : HoleEndStyle.THROUGH, "holeDiameter" : 14 * mm, "cSinkDiameter" : 16 * mm, "cSinkAngle" : 90 * degree, "majorDiameter" : 8 * mm, "isTappedThrough" : true, "tappedDepth" : 31.25 * mm, "tapClearance" : 3, "startFromSketch" : true, "locations" : qUnion([Q0]), "scope" : qUnion([Q1])});
        }
        {
            var Q0;
            Q0=makeQuery(id+"F3.opExtrude","CAP_FACE",FACE,{"disambiguationData":[OSD([sQuery(id+"F2.wireOp",EDGE,"E15")])],"isStart":false});
            var sketch = newSketch(context, id + "F21", { "sketchPlane" : qUnion([Q0])});
            skCircle(sketch, "E40", {"center": v(0, 0) * mm, "radius": 7.5 * mm});
            skSolve(sketch);
        }
        {
            var Q0;
            Q0 = qSketchRegion(id + "F21", true);
            extrude(context, id + "F22", {"entities" : qUnion([Q0]), "operationType" : NewBodyOperationType.REMOVE, "oppositeDirection" : true, "depth" : 7 * mm, "offsetDistance" : 25 * mm});
        }
    });
